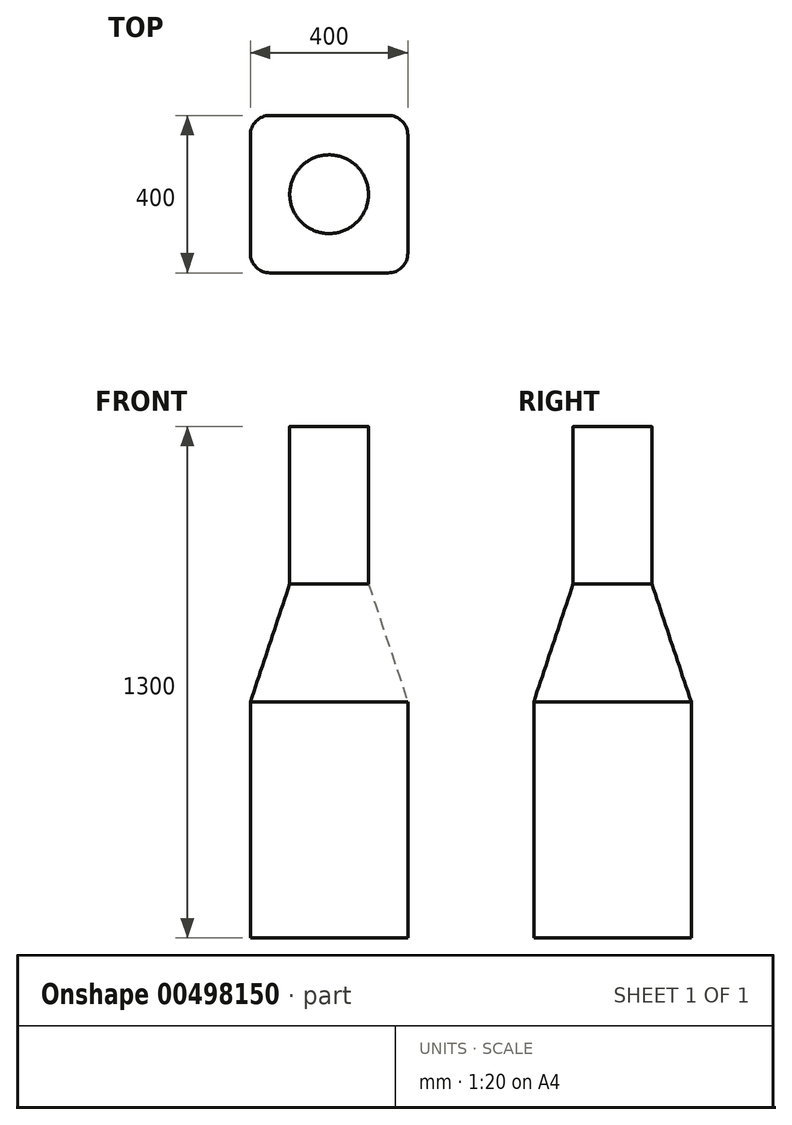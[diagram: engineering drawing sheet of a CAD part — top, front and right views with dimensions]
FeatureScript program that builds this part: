
annotation { "Feature Type Name" : "Feature", "Feature Type Description" : "" }
export const myFeature = defineFeature(function(context is Context, id is Id, definition is map)
    precondition{}
    {
        {
            var Q0;
            Q0=qCreatedBy(makeId("Front.planeOp"),FACE);
            var sketch = newSketch(context, id + "F0", { "sketchPlane" : qUnion([Q0])});
            skLineSegment(sketch, "E0", {"start": v(0, 0.06) * mm, "end": v(0, 36.07) * mm});
            skLineSegment(sketch, "E1", {"start": v(2.49, 38.1) * mm, "end": v(3.38, 38.1) * mm});
            skLineSegment(sketch, "E2", {"start": v(3.89, 37.63) * mm, "end": v(6.2, 8.18) * mm});
            skArc(sketch, "E3", {"start": v(6.2, 8.18) * mm, "mid": v(6.9, 6.43) * mm, "end": v(8.48, 5.39) * mm});
            skLineSegment(sketch, "E4", {"start": v(8.48, 5.39) * mm, "end": v(16.46, 3.05) * mm});
            skArc(sketch, "E5", {"start": v(18.75, 0) * mm, "mid": v(18.11, 1.9) * mm, "end": v(16.46, 3.05) * mm});
            skLineSegment(sketch, "E6", {"start": v(18.75, 0) * mm, "end": v(0, 0) * mm});
            skArc(sketch, "E7", {"start": v(0, 36.07) * mm, "mid": v(1.6, 36.64) * mm, "end": v(2.49, 38.1) * mm});
            skArc(sketch, "E8.filletArc", {"start": v(3.89, 37.63) * mm, "mid": v(3.73, 37.97) * mm, "end": v(3.38, 38.1) * mm});
            skSolve(sketch);
        }
        {
            var Q0;
            Q0 = qSketchRegion(id + "F0", true);
            var Q1;
            Q1=sQuery(id+"F0.wireOp",EDGE,"E7");
            var Q2;
            Q2=sQuery(id+"F0.wireOp",EDGE,"E1");
            var Q3;
            Q3=sQuery(id+"F0.wireOp",EDGE,"E8.filletArc");
            var Q4;
            Q4=sQuery(id+"F0.wireOp",EDGE,"E2");
            var Q5;
            Q5=sQuery(id+"F0.wireOp",EDGE,"E3");
            var Q6;
            Q6=sQuery(id+"F0.wireOp",EDGE,"E4");
            var Q7;
            Q7=sQuery(id+"F0.wireOp",EDGE,"E5");
            var Q8;
            Q8=sQuery(id+"F0.wireOp",EDGE,"E6");
            var Q9;
            Q9=sQuery(id+"F0.wireOp",EDGE,"E0");
            revolve(context, id + "F1", {"bodyType" : ToolBodyType.SURFACE, "entities" : qUnion([Q0]), "surfaceEntities" : qUnion([Q1, Q2, Q3, Q4, Q5, Q6, Q7, Q8]), "axis" : qUnion([Q9]), "revolveType" : RevolveType.FULL});
        }
        {
            var Q0;
            Q0=qCreatedBy(makeId("Top.planeOp"),FACE);
            var sketch = newSketch(context, id + "F2", { "sketchPlane" : qUnion([Q0])});
            skLineSegment(sketch, "E9.bottom", {"start": v(658, 200) * mm, "end": v(358, 200) * mm});
            skLineSegment(sketch, "E9.top", {"start": v(658, -200) * mm, "end": v(358, -200) * mm});
            skLineSegment(sketch, "E9.left", {"start": v(708, 150) * mm, "end": v(708, -150) * mm});
            skLineSegment(sketch, "E9.right", {"start": v(308, 150) * mm, "end": v(308, -150) * mm});
            skPoint(sketch, "E9.middle", {"position": v(508, 0) * mm});
            skPoint(sketch, "E10.visualSharp", {"position": v(308, 200) * mm});
            skArc(sketch, "E10.filletArc", {"start": v(358, 200) * mm, "mid": v(322.64, 185.36) * mm, "end": v(308, 150) * mm});
            skPoint(sketch, "E11.visualSharp", {"position": v(708, 200) * mm});
            skArc(sketch, "E11.filletArc", {"start": v(708, 150) * mm, "mid": v(693.36, 185.36) * mm, "end": v(658, 200) * mm});
            skPoint(sketch, "E12.visualSharp", {"position": v(708, -200) * mm});
            skArc(sketch, "E12.filletArc", {"start": v(658, -200) * mm, "mid": v(693.36, -185.36) * mm, "end": v(708, -150) * mm});
            skPoint(sketch, "E13.visualSharp", {"position": v(308, -200) * mm});
            skArc(sketch, "E13.filletArc", {"start": v(308, -150) * mm, "mid": v(322.64, -185.36) * mm, "end": v(358, -200) * mm});
            skSolve(sketch);
        }
        {
            var Q0;
            Q0=qCreatedBy(makeId("Top.planeOp"),FACE);
            cPlane(context, id + "F3", {"entities" : qUnion([Q0]), "cplaneType" : CPlaneType.OFFSET, "offset" : 600 * mm, "width" : 152.4 * mm, "height" : 152.4 * mm});
        }
        {
            var Q0;
            Q0=qCreatedBy(id+"F3.planeOp",FACE);
            cPlane(context, id + "F4", {"entities" : qUnion([Q0]), "cplaneType" : CPlaneType.OFFSET, "offset" : 300 * mm, "width" : 152.4 * mm, "height" : 152.4 * mm});
        }
        {
            var Q0;
            Q0=qCreatedBy(id+"F4.planeOp",FACE);
            cPlane(context, id + "F5", {"entities" : qUnion([Q0]), "cplaneType" : CPlaneType.OFFSET, "offset" : 400 * mm, "width" : 152.4 * mm, "height" : 152.4 * mm});
        }
        {
            var Q0;
            Q0=qCreatedBy(id+"F3.planeOp",FACE);
            var sketch = newSketch(context, id + "F6", { "sketchPlane" : qUnion([Q0])});
            skLineSegment(sketch, "E14.0", {"start": v(658, 200) * mm, "end": v(358, 200) * mm});
            skLineSegment(sketch, "E14.1", {"start": v(658, -200) * mm, "end": v(358, -200) * mm});
            skLineSegment(sketch, "E14.2", {"start": v(708, 150) * mm, "end": v(708, -150) * mm});
            skLineSegment(sketch, "E14.3", {"start": v(308, 150) * mm, "end": v(308, -150) * mm});
            skArc(sketch, "E14.4", {"start": v(358, 200) * mm, "mid": v(322.64, 185.36) * mm, "end": v(308, 150) * mm});
            skArc(sketch, "E14.5", {"start": v(708, 150) * mm, "mid": v(693.36, 185.36) * mm, "end": v(658, 200) * mm});
            skArc(sketch, "E14.6", {"start": v(658, -200) * mm, "mid": v(693.36, -185.36) * mm, "end": v(708, -150) * mm});
            skArc(sketch, "E14.7", {"start": v(308, -150) * mm, "mid": v(322.64, -185.36) * mm, "end": v(358, -200) * mm});
            skSolve(sketch);
        }
        {
            var Q0;
            Q0=qCreatedBy(id+"F4.planeOp",FACE);
            var sketch = newSketch(context, id + "F7", { "sketchPlane" : qUnion([Q0])});
            skPoint(sketch, "E15.0", {"position": v(508, 0) * mm});
            skCircle(sketch, "E16", {"center": v(508, 0) * mm, "radius": 100 * mm});
            skSolve(sketch);
        }
        {
            var Q0;
            Q0=qCreatedBy(id+"F5.planeOp",FACE);
            var sketch = newSketch(context, id + "F8", { "sketchPlane" : qUnion([Q0])});
            skCircle(sketch, "E17.0", {"center": v(508, 0) * mm, "radius": 100 * mm});
            skSolve(sketch);
        }
        {
            var Q0;
            Q0=makeQuery(id+"F2.imprint","IMPRINT",FACE,{"disambiguationData":[TD([[makeQuery(id+"F2.imprint","IMPRINT",EDGE,{"derivedFrom":sQuery(id+"F2.wireOp",EDGE,"E9.bottom")}),1.0]])]});
            var Q1;
            Q1=makeQuery(id+"F6.imprint","IMPRINT",FACE,{"disambiguationData":[TD([[makeQuery(id+"F6.imprint","IMPRINT",EDGE,{"derivedFrom":sQuery(id+"F6.wireOp",EDGE,"E14.0")}),1.0]])]});
            loft(context, id + "F9", {"sheetProfilesArray" : [{ "sheetProfileEntities" : qUnion([Q0]) }, { "sheetProfileEntities" : qUnion([Q1]) }]});
        }
        {
            var Q1;
            Q1=makeQuery(id+"F9.opLoft","CAP_FACE",FACE,{"disambiguationData":[OSD([makeQuery(id+"F6.imprint","IMPRINT",FACE,{"disambiguationData":[TD([[makeQuery(id+"F6.imprint","IMPRINT",EDGE,{"derivedFrom":sQuery(id+"F6.wireOp",EDGE,"E14.0")}),1.0]])]})])],"isStart":true});
            var Q2;
            Q2=makeQuery(id+"F7.imprint","IMPRINT",FACE,{"disambiguationData":[TD([[makeQuery(id+"F7.imprint","IMPRINT",EDGE,{"derivedFrom":sQuery(id+"F7.wireOp",EDGE,"E16")}),1.0]])]});
            loft(context, id + "F10", {"operationType" : NewBodyOperationType.ADD, "sheetProfilesArray" : [{ "sheetProfileEntities" : qUnion([Q1]) }, { "sheetProfileEntities" : qUnion([Q2]) }]});
        }
        {
            var Q1;
            Q1=makeQuery(id+"F10.opLoft","CAP_FACE",FACE,{"disambiguationData":[OSD([makeQuery(id+"F7.imprint","IMPRINT",FACE,{"disambiguationData":[TD([[makeQuery(id+"F7.imprint","IMPRINT",EDGE,{"derivedFrom":sQuery(id+"F7.wireOp",EDGE,"E16")}),1.0]])]})])],"isStart":true});
            var Q2;
            Q2=makeQuery(id+"F8.imprint","IMPRINT",FACE,{"disambiguationData":[TD([[makeQuery(id+"F8.imprint","IMPRINT",EDGE,{"derivedFrom":sQuery(id+"F8.wireOp",EDGE,"E17.0")}),1.0]])]});
            loft(context, id + "F11", {"operationType" : NewBodyOperationType.ADD, "sheetProfilesArray" : [{ "sheetProfileEntities" : qUnion([Q1]) }, { "sheetProfileEntities" : qUnion([Q2]) }]});
        }
    });
